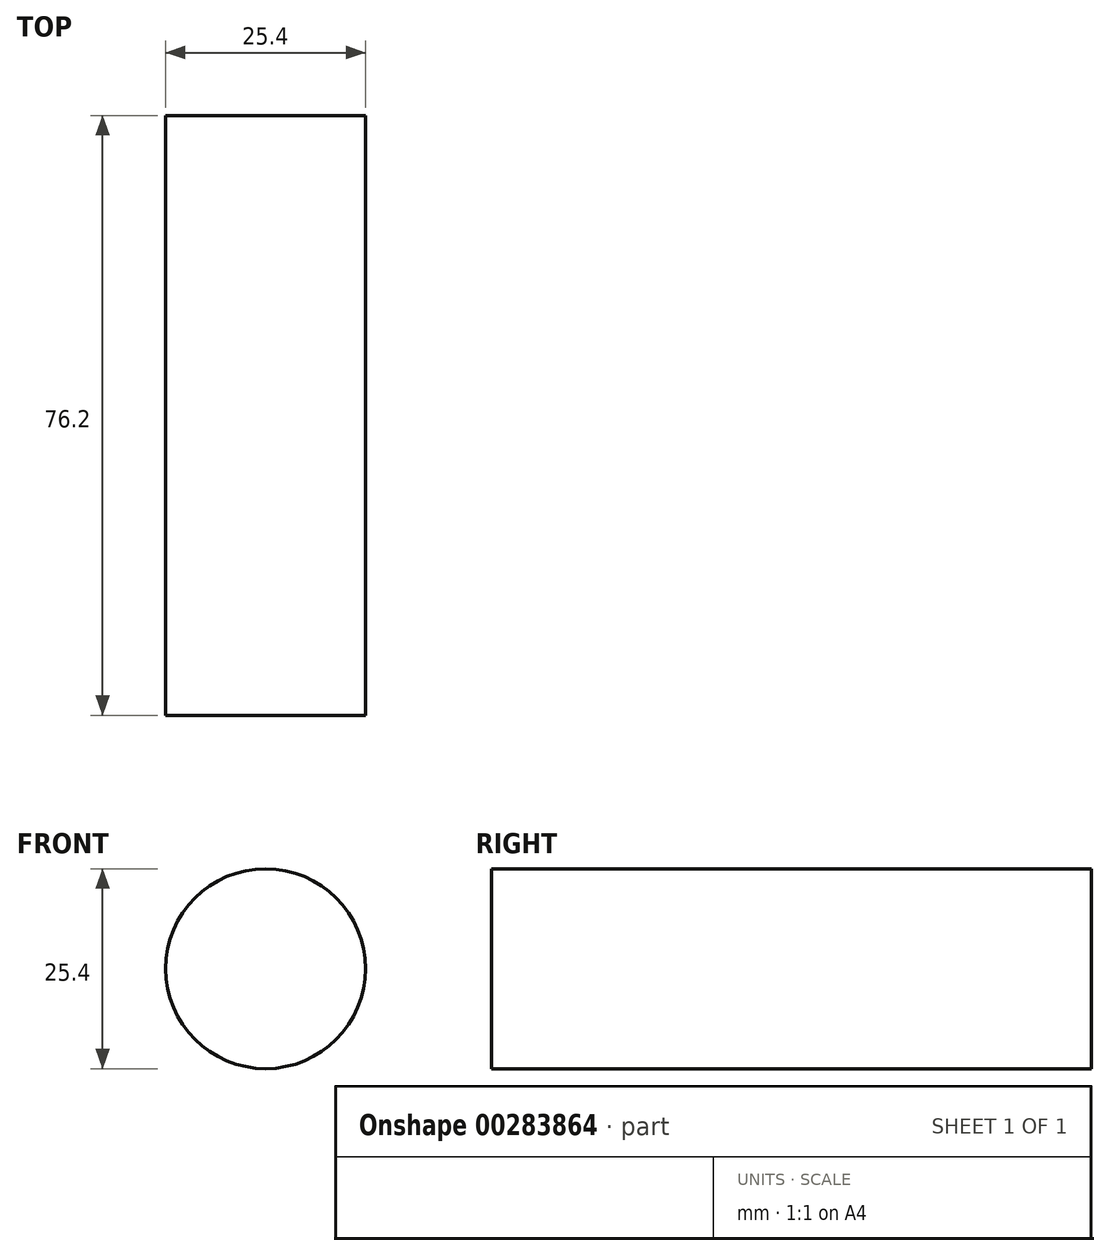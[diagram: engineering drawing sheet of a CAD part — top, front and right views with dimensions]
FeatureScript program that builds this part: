
annotation { "Feature Type Name" : "Feature", "Feature Type Description" : "" }
export const myFeature = defineFeature(function(context is Context, id is Id, definition is map)
    precondition{}
    {
        {
            var Q0;
            Q0=qCreatedBy(makeId("Front.planeOp"),FACE);
            var sketch = newSketch(context, id + "F0", { "sketchPlane" : qUnion([Q0])});
            skCircle(sketch, "E0", {"center": v(-23.1, 26.16) * mm, "radius": 12.7 * mm});
            skSolve(sketch);
        }
        {
            var Q0;
            Q0 = qSketchRegion(id + "F0", true);
            extrude(context, id + "F1", {"entities" : qUnion([Q0]), "depth" : 76.2 * mm});
        }
    });
